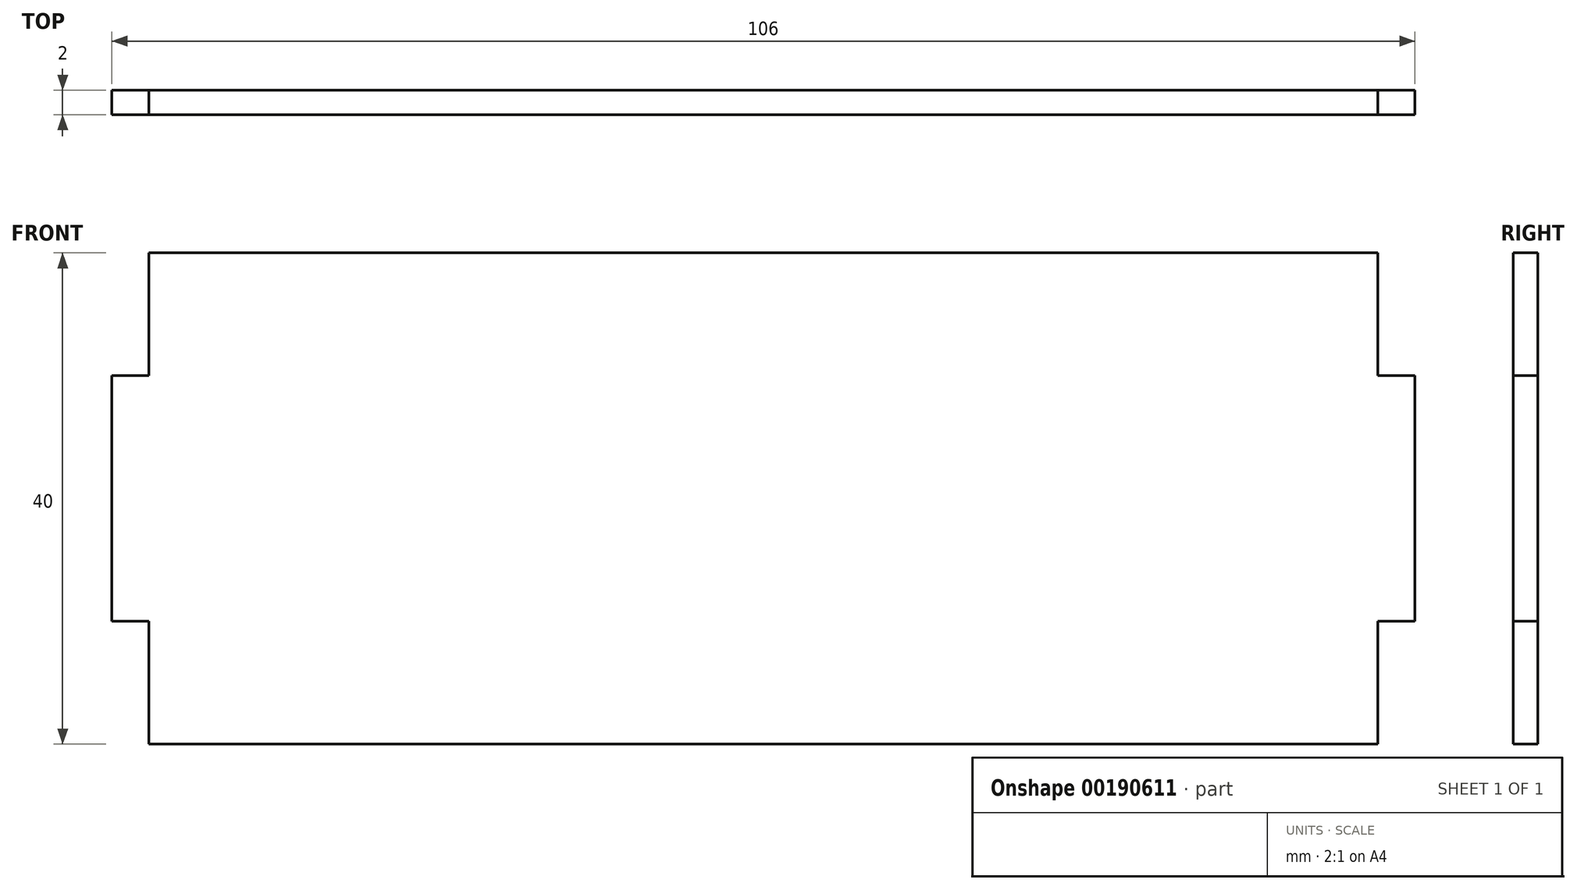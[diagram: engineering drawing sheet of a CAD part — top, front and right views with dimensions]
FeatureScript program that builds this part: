
annotation { "Feature Type Name" : "Feature", "Feature Type Description" : "" }
export const myFeature = defineFeature(function(context is Context, id is Id, definition is map)
    precondition{}
    {
        {
            var Q0;
            Q0=qCreatedBy(makeId("Front.planeOp"),FACE);
            var sketch = newSketch(context, id + "F0", { "sketchPlane" : qUnion([Q0])});
            skLineSegment(sketch, "E0.bottom", {"start": v(50, 20) * mm, "end": v(-50, 20) * mm});
            skLineSegment(sketch, "E0.top", {"start": v(50, -20) * mm, "end": v(-50, -20) * mm});
            skLineSegment(sketch, "E0.left", {"start": v(50, 20) * mm, "end": v(50, 10) * mm});
            skPoint(sketch, "E0.middle", {"position": v(0, 0) * mm});
            skLineSegment(sketch, "E1.bottom", {"start": v(50, -10) * mm, "end": v(53, -10) * mm});
            skLineSegment(sketch, "E1.top", {"start": v(50, 10) * mm, "end": v(53, 10) * mm});
            skLineSegment(sketch, "E1.right", {"start": v(53, -10) * mm, "end": v(53, 10) * mm});
            skLineSegment(sketch, "E2", {"start": v(0, 20) * mm, "end": v(0, -20) * mm, "construction": true});
            skLineSegment(sketch, "E3", {"start": v(50, -10) * mm, "end": v(50, -20) * mm});
            skLineSegment(sketch, "E4.MirrorCS", {"start": v(-50, 20) * mm, "end": v(-50, 10) * mm});
            skLineSegment(sketch, "E5.MirrorCS", {"start": v(-50, -10) * mm, "end": v(-50, -20) * mm});
            skLineSegment(sketch, "E6.MirrorCS", {"start": v(-53, -10) * mm, "end": v(-53, 10) * mm});
            skLineSegment(sketch, "E7.MirrorCS", {"start": v(-50, -10) * mm, "end": v(-53, -10) * mm});
            skLineSegment(sketch, "E8.MirrorCS", {"start": v(-50, 10) * mm, "end": v(-53, 10) * mm});
            skSolve(sketch);
        }
        {
            var Q0;
            Q0=makeQuery(id+"F0.imprint","IMPRINT",FACE,{"disambiguationData":[TD([[makeQuery(id+"F0.imprint","IMPRINT",EDGE,{"derivedFrom":sQuery(id+"F0.wireOp",EDGE,"E0.bottom")}),1.0]])]});
            extrude(context, id + "F1", {"entities" : qUnion([Q0]), "depth" : 2 * mm});
        }
    });
